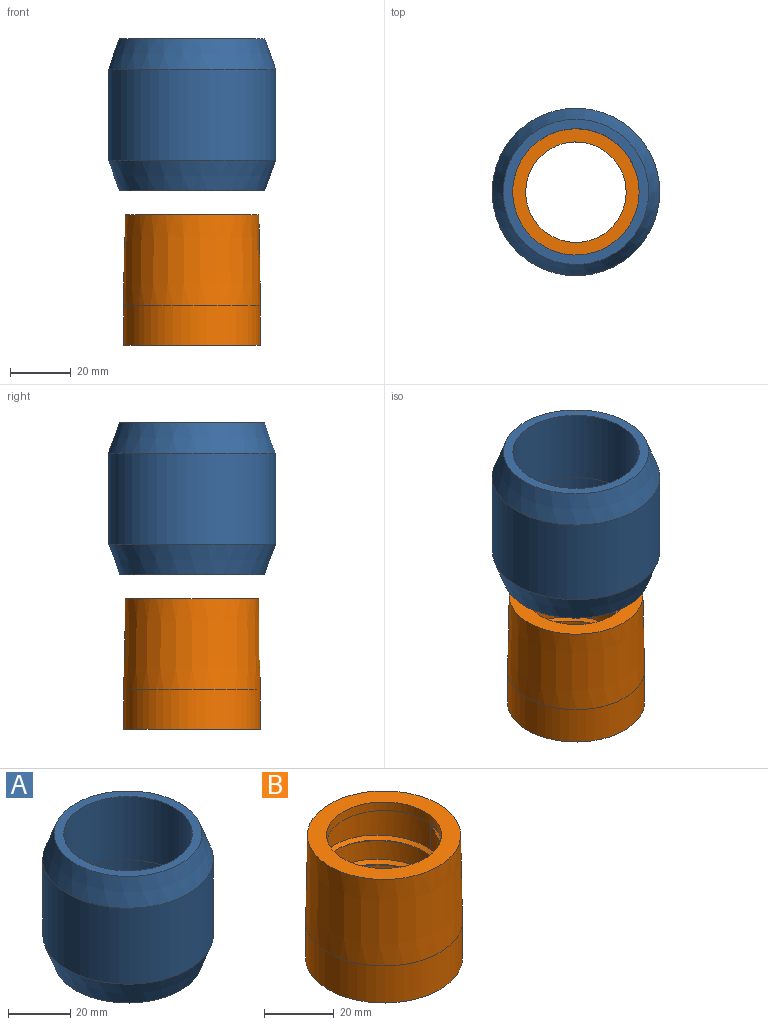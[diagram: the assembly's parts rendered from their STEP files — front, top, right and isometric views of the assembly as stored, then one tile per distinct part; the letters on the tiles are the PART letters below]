
ASSEMBLY  parts=2 mates=1
PART A: 8 faces, bbox 55x55x50 mm
  f0: cylinder r=22.9mm len=45.8mm, axis (0,0,-1), area 3597.1mm2, adj f2,f3
  f1: cylinder r=27.5mm len=55mm, axis (0,0,-1), area 5183.6mm2, adj f6,f7
  f2: plane 47.72x47.72mm, normal (0,0,-1), area 141.1mm2, adj f0,f7
  f3: plane 45.8x45.8mm, normal (0,0,-1), area 294.8mm2, adj f0,f4
  f4: cylinder r=20.75mm len=41.5mm, axis (0,0,-1), area 3259.4mm2, adj f3,f5
  f5: plane 47.72x47.72mm, normal (0,0,1), area 435.9mm2, adj f4,f6
  f6: cone r=23.86mm half-angle=20deg, axis (0,0,-1), area 1717.1mm2, adj f1,f5
  f7: cone r=27.5mm half-angle=20deg, axis (0,0,1), area 1717.1mm2, adj f1,f2
PART B: 17 faces, bbox 45x45x43.2 mm
  f0: cylinder r=19mm len=12.77mm, axis (0,0,-1), area 7mm2, adj f1,f7,f10
  f1: cylinder r=19mm len=38mm, axis (0,0,-1), area 596.3mm2, adj f0,f2,f7,f9,f10,f11
  f2: cylinder r=19mm len=38mm, axis (0,0,-1), area 776mm2, adj f1,f3,f9,f10
  f3: cylinder r=19mm len=38mm, axis (0,0,-1), area 776mm2, adj f2,f4,f9,f10
  f4: cylinder r=19mm len=38mm, axis (0,0,-1), area 780.6mm2, adj f3,f5,f9,f10,f16
  f5: cylinder r=19mm len=38mm, axis (0,0,-1), area 865.4mm2, adj f4,f8,f9,f12
  f6: cylinder r=22.5mm len=45mm, axis (0,0,-1), area 1837.8mm2, adj f7,f15
  f7: plane 45x45mm, normal (0,0,-1), area 456.3mm2, adj f0,f1,f6
  f8: plane 0.09x0.05mm, normal (0,1,0), area 0mm2, adj f5,f9,f16
  f9: bspline ~38x38mm, area 710.5mm2, adj f1,f2,f3,f4,f5,f8,f10,f11
  f10: bspline ~38x38mm, area 702mm2, adj f0,f1,f2,f3,f4,f9,f11,f16
  f11: bspline ~5.69x3.92mm, area 4mm2, adj f1,f9,f10
  f12: plane 38x38mm, normal (0,0,-1), area 278.8mm2, adj f5,f13
  f13: cylinder r=16.5mm len=33mm, axis (0,0,-1), area 311mm2, adj f12,f14
  f14: plane 43.95x43.95mm, normal (0,0,1), area 662mm2, adj f13,f15
  f15: cone r=21.98mm half-angle=1deg, axis (0,0,-1), area 4192.4mm2, adj f6,f14
  f16: bspline ~4.65x2.85mm, area 4.3mm2, adj f4,f8,f9,f10
PLACE A t=(-90.11,-102.75,23.77)mm
PLACE B t=(-90.11,-102.75,-27.02)mm
MATE slider B.f13 <-> A.f0  axis (0,0,1) through (-90.11,-102.75,15.98)mm
